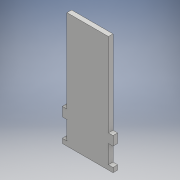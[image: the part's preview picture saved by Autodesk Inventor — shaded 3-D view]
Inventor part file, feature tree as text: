
AUTODESK INVENTOR PART (.ipt)
format: ipt  version: 2017 (Build 210142000, 142)  size: 121,856 bytes
history: native  units: mm
features: extrude x1, sketch x1
ambient origin geometry x8: Origin, YZ Plane, XZ Plane, XY Plane, X Axis, Y Axis, Z Axis, Center Point
bodies: Solid1 (feature_tree)
feature tree (2):
  extrude  "Extrusion1"  Depth=3.0mm
  sketch  "Sketch1"  dims[d2=3.0mm d3=0.0mm d8=3.0mm d9=3.0mm d11=33.0mm d12=6.0mm d13=60.415173mm d14=12.0mm]
